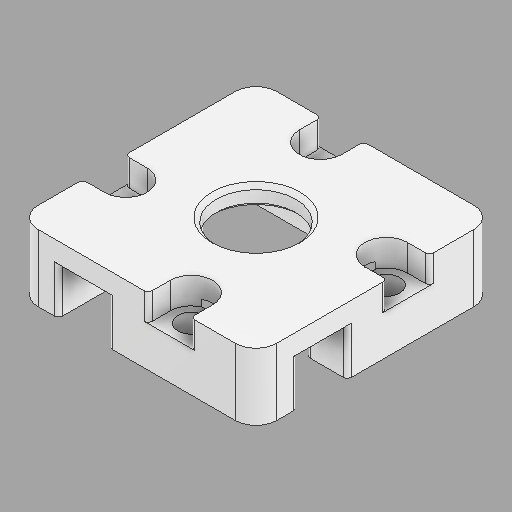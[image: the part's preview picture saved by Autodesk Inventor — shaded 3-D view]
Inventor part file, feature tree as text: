
AUTODESK INVENTOR PART (.ipt)
format: ipt  version: 2024.2 (Build 282272000, 272)  size: 174,080 bytes
history: native  units: in
note: dims shown in document units (in); Inventor stores cm internally (conversion verified against a paired STEP export)
features: fillet x1
ambient origin geometry x8: Origin, YZ Plane, XZ Plane, XY Plane, X Axis, Y Axis, Z Axis, Center Point
bodies: Solid1 (feature_tree)
feature tree (1):
  fillet  "Fillet4"  [1 undecoded]
note: 1 required parameter value undecoded (feature->parameter linkage not recoverable at this tier; creation-order binding heuristic only, values carry confidence <= 0.55)
